# Revit family: Automatic air vents 2630 03
name_source: partatom
category: Rohrzubehör
units: mm (PartAtom-declared; Revit-internal decimal feet)

## family parameters
Arbeitsebenenbasiert = Nein
Beim Laden mit Abzugskörper schneiden = Nein
Bemaßung runder Anschluss = Durchmesser verwenden
Gemeinsam genutzt = Nein
Immer vertikal = Ja
OmniClass-Nummer = 23.65.55.14
OmniClass-Titel = Valves for Liquid Services
Teiletyp = Normal

## types (1)
- Automatic air vents 2630 03
    Adapter housing = machined brass acc. to EN 12165, CW617N
    Cover cap = polypropylene, black colour
    D01 = 16.2 mm  [stored 0.0531496 ft]
    D02 = 19.5 mm  [stored 0.0639764 ft]
    D03 = 5.1 mm  [stored 0.0167323 ft]
    D04 = 3.4 mm  [stored 0.0111549 ft]
    D05 = 0.8 mm  [stored 0.00262467 ft]
    D06 = 13.5 mm  [stored 0.0442913 ft]
    External threaded connectors = acc. to ISO 228
    Field of application = HERZ - Air vent is used for venting of the central heating installations.
the air vent should be placed nearby the boiler or at the highest points of installation.
installations must be carried out in such a way that the retention of air bubbles in a certain part of installation is not possible.
before usage, unscrew the polypropylene cover cap on the lid for 2 to 3 turns.
in case of uncontrolled medium leakage, tighten the cover cap.
the air vent must be cleaned or replaced.
we always recommend to use backflow preventer for easy service and replacement of the air vent.
    Float ball = polypropylene
    G1 = 5 mm  [stored 0.0164042 ft]
    H00 = 71.5 mm
    H01 = 12 mm  [stored 0.0393701 ft]
    H02 = 9.5 mm  [stored 0.031168 ft]
    H03 = 63 mm  [stored 0.206693 ft]
    H04 = 57.9 mm  [stored 0.189961 ft]
    H05 = 58 mm  [stored 0.190289 ft]
    H06 = 14 mm  [stored 0.0459318 ft]
    H07 = 22 mm  [stored 0.0721785 ft]
    H08 = 8 mm  [stored 0.0262467 ft]
    Hersteller = Herz-Armaturen GmbH
    Housing = forged brass acc. to EN 12165, CW617N
    L00 = 33.5 mm
    L01 = 9.5 mm  [stored 0.031168 ft]
    L02 = 4.8 mm  [stored 0.015748 ft]
    L03 = 13.5 mm  [stored 0.0442913 ft]
    L04 = 24 mm  [stored 0.0787402 ft]
    Lid = forged brass acc. to EN 12165, CW617N
    Medium = heating water quality according to ÖNORM H5195 or VDI-Standard 2035.
the use of ethylene or propylene glycol in a mixing ratio 25-50% is allowed.
please refer to manufacturers documentation when using ethylene glycol products for frost and corrosion protection.
the HERZ air vent is not suitable for usage of aggressive medium (such as: acids, alkalis, combustible and explosive gases..) because it can damage the sealing components.
    R01 = 2 mm  [stored 0.00656168 ft]
    S01 = 59 mm
    S02 = 12.5 mm  [stored 0.0410105 ft]
    S03 = 24.5 mm  [stored 0.0803806 ft]
    S04 = 11 mm  [stored 0.0360892 ft]
    SCRNCODE = 05;14;01
    SCRNSEQ = AWI;AWI_TYP="1013";1
    Sealing = NBR
    URL = www.herzvalves.com
    Vorgabe-Ansicht = 0 mm  [stored 0 ft]
    max. Operating pressure = 800000.0 Pa
    max. Operating temperature = 110 °C
    max. Structual pressure = 1200000.0 Pa
    min. Operating temperature = 0 °C

note: [stored X ft] marks values corroborated as IEEE doubles in the binary element streams (Revit-internal decimal feet)
